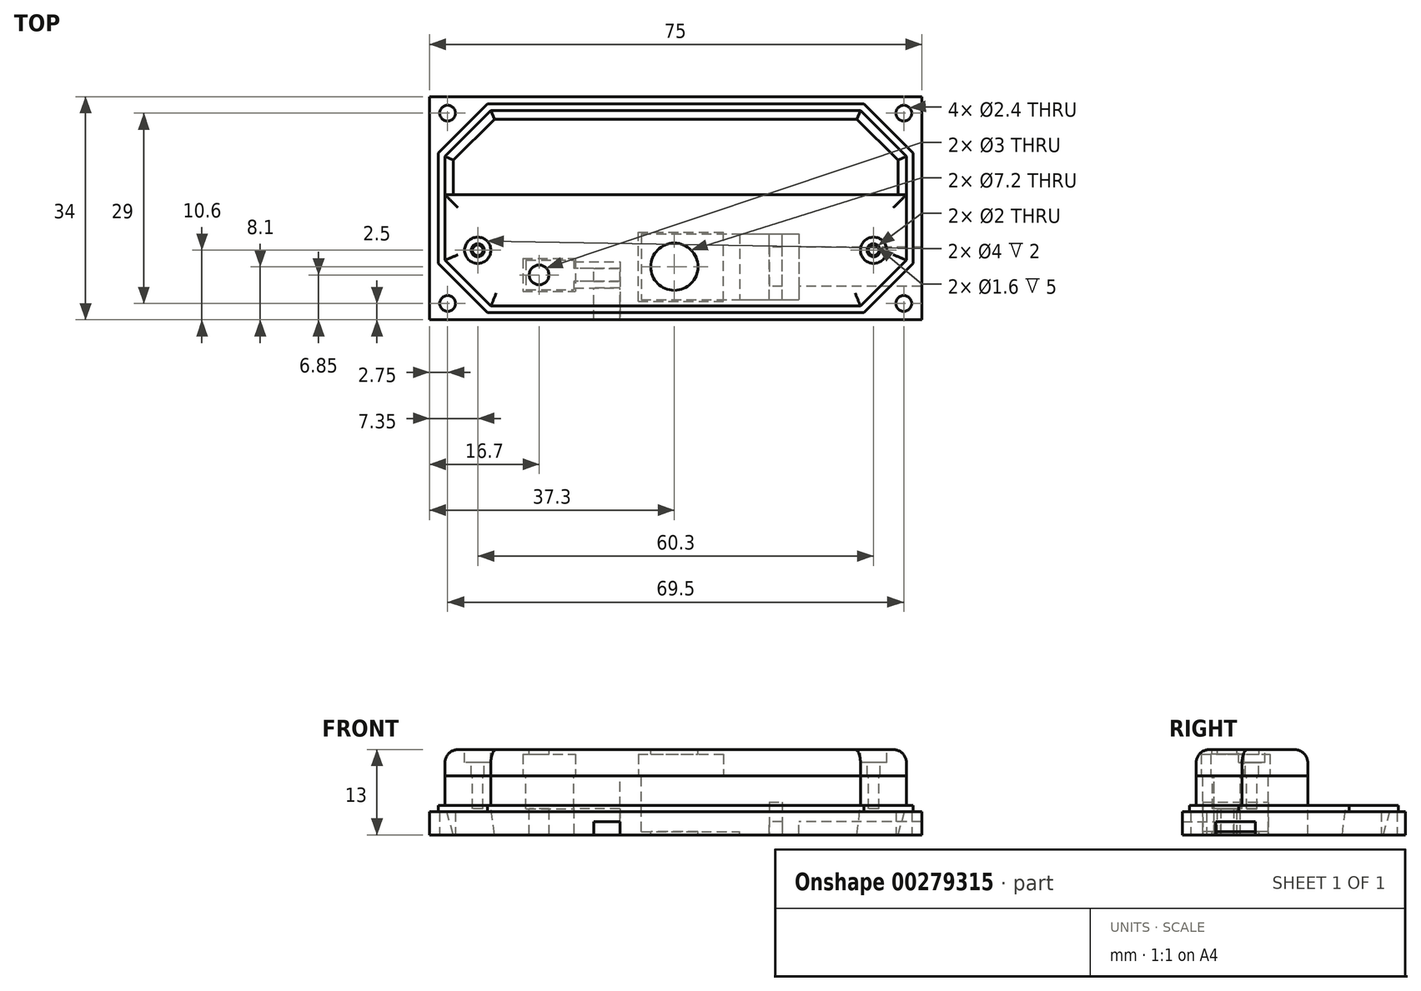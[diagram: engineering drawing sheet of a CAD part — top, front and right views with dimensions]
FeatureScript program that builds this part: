
annotation { "Feature Type Name" : "Feature", "Feature Type Description" : "" }
export const myFeature = defineFeature(function(context is Context, id is Id, definition is map)
    precondition{}
    {
        {
            var Q0;
            Q0=qCreatedBy(makeId("Top.planeOp"),FACE);
            var sketch = newSketch(context, id + "F0", { "sketchPlane" : qUnion([Q0])});
            skLineSegment(sketch, "E0.bottom", {"start": v(37.5, -17) * mm, "end": v(-37.5, -17) * mm});
            skLineSegment(sketch, "E0.top", {"start": v(37.5, 17) * mm, "end": v(-37.5, 17) * mm});
            skLineSegment(sketch, "E0.left", {"start": v(37.5, -17) * mm, "end": v(37.5, 17) * mm});
            skLineSegment(sketch, "E0.right", {"start": v(-37.5, -17) * mm, "end": v(-37.5, 17) * mm});
            skPoint(sketch, "E0.middle", {"position": v(0, 0) * mm});
            skLineSegment(sketch, "E1.bottom", {"start": v(-28.65, 15.9) * mm, "end": v(28.65, 15.9) * mm, "construction": true});
            skLineSegment(sketch, "E1.top", {"start": v(-28.65, -15.9) * mm, "end": v(28.65, -15.9) * mm, "construction": true});
            skLineSegment(sketch, "E1.left", {"start": v(-36.15, 8.4) * mm, "end": v(-36.15, -8.4) * mm, "construction": true});
            skLineSegment(sketch, "E1.right", {"start": v(36.15, 8.4) * mm, "end": v(36.15, -8.4) * mm, "construction": true});
            skLineSegment(sketch, "E2", {"start": v(-36.15, 8.4) * mm, "end": v(-28.65, 15.9) * mm, "construction": true});
            skLineSegment(sketch, "E3", {"start": v(28.65, 15.9) * mm, "end": v(36.15, 8.4) * mm, "construction": true});
            skLineSegment(sketch, "E4", {"start": v(36.15, -8.4) * mm, "end": v(28.65, -15.9) * mm, "construction": true});
            skLineSegment(sketch, "E5", {"start": v(-36.15, -8.4) * mm, "end": v(-28.65, -15.9) * mm, "construction": true});
            skCircle(sketch, "E6", {"center": v(-34.75, 14.5) * mm, "radius": 1.2 * mm});
            skCircle(sketch, "E7", {"center": v(34.75, 14.5) * mm, "radius": 1.2 * mm});
            skCircle(sketch, "E8", {"center": v(-34.75, -14.5) * mm, "radius": 1.2 * mm});
            skCircle(sketch, "E9", {"center": v(34.75, -14.5) * mm, "radius": 1.2 * mm});
            skLineSegment(sketch, "E10", {"start": v(0, -47.1) * mm, "end": v(0, -78.86) * mm, "construction": true});
            skSolve(sketch);
        }
        {
            var Q0;
            Q0 = qSketchRegion(id + "F0", true);
            extrude(context, id + "F1", {"entities" : qUnion([Q0]), "depth" : 3.5 * mm});
        }
        {
            var Q0;
            Q0=makeQuery(id+"F1.opExtrude","CAP_FACE",FACE,{"disambiguationData":[OSD([sQuery(id+"F0.wireOp",EDGE,"E0.bottom"),sQuery(id+"F0.wireOp",EDGE,"E0.top"),sQuery(id+"F0.wireOp",EDGE,"E0.left"),sQuery(id+"F0.wireOp",EDGE,"E0.right"),sQuery(id+"F0.wireOp",EDGE,"E6"),sQuery(id+"F0.wireOp",EDGE,"E7"),sQuery(id+"F0.wireOp",EDGE,"E8"),sQuery(id+"F0.wireOp",EDGE,"E9")])],"isStart":false});
            var sketch = newSketch(context, id + "F2", { "sketchPlane" : qUnion([Q0])});
            skLineSegment(sketch, "E11.bottom", {"start": v(-28.65, 15.9) * mm, "end": v(28.65, 15.9) * mm});
            skLineSegment(sketch, "E11.top", {"start": v(-28.65, -15.9) * mm, "end": v(28.65, -15.9) * mm});
            skLineSegment(sketch, "E11.left", {"start": v(-36.15, 8.4) * mm, "end": v(-36.15, -8.4) * mm});
            skLineSegment(sketch, "E11.right", {"start": v(36.15, 8.4) * mm, "end": v(36.15, -8.4) * mm});
            skLineSegment(sketch, "E12", {"start": v(-36.15, 8.4) * mm, "end": v(-28.65, 15.9) * mm});
            skLineSegment(sketch, "E13", {"start": v(28.65, 15.9) * mm, "end": v(36.15, 8.4) * mm});
            skLineSegment(sketch, "E14", {"start": v(36.15, -8.4) * mm, "end": v(28.65, -15.9) * mm});
            skLineSegment(sketch, "E15", {"start": v(-36.15, -8.4) * mm, "end": v(-28.65, -15.9) * mm});
            skSolve(sketch);
        }
        {
            var Q0;
            Q0 = qSketchRegion(id + "F2", true);
            extrude(context, id + "F3", {"entities" : qUnion([Q0]), "operationType" : NewBodyOperationType.ADD, "depth" : 1 * mm});
        }
        {
            var Q0;
            Q0=makeQuery(id+"F3.opExtrude","CAP_FACE",FACE,{"disambiguationData":[OSD([sQuery(id+"F2.wireOp",EDGE,"E11.bottom"),sQuery(id+"F2.wireOp",EDGE,"E11.top"),sQuery(id+"F2.wireOp",EDGE,"E11.left"),sQuery(id+"F2.wireOp",EDGE,"E11.right"),sQuery(id+"F2.wireOp",EDGE,"E12"),sQuery(id+"F2.wireOp",EDGE,"E13"),sQuery(id+"F2.wireOp",EDGE,"E14"),sQuery(id+"F2.wireOp",EDGE,"E15")])],"isStart":false});
            var sketch = newSketch(context, id + "F4", { "sketchPlane" : qUnion([Q0])});
            skLineSegment(sketch, "E16.bottom", {"start": v(-28.15, 14.9) * mm, "end": v(28.15, 14.9) * mm});
            skLineSegment(sketch, "E16.top", {"start": v(-28.15, -14.9) * mm, "end": v(28.15, -14.9) * mm});
            skLineSegment(sketch, "E16.left", {"start": v(-35.15, 7.9) * mm, "end": v(-35.15, -7.9) * mm});
            skLineSegment(sketch, "E16.right", {"start": v(35.15, 7.9) * mm, "end": v(35.15, -7.9) * mm});
            skLineSegment(sketch, "E17", {"start": v(-35.15, 7.9) * mm, "end": v(-28.15, 14.9) * mm});
            skLineSegment(sketch, "E18", {"start": v(28.15, 14.9) * mm, "end": v(35.15, 7.9) * mm});
            skLineSegment(sketch, "E19", {"start": v(35.15, -7.9) * mm, "end": v(28.15, -14.9) * mm});
            skLineSegment(sketch, "E20", {"start": v(-35.15, -7.9) * mm, "end": v(-28.15, -14.9) * mm});
            skSolve(sketch);
        }
        {
            var Q0;
            Q0 = qSketchRegion(id + "F4", true);
            extrude(context, id + "F5", {"entities" : qUnion([Q0]), "operationType" : NewBodyOperationType.REMOVE, "oppositeDirection" : true, "depth" : 5 * mm});
        }
        {
            var Q0;
            Q0=qCreatedBy(makeId("Front.planeOp"),FACE);
            cPlane(context, id + "F6", {"entities" : qUnion([Q0]), "cplaneType" : CPlaneType.OFFSET, "offset" : 2.1 * mm, "oppositeDirection" : true, "width" : 150 * mm, "height" : 150 * mm});
        }
        {
            var Q0;
            Q0=qCreatedBy(id+"F6.planeOp",FACE);
            var sketch = newSketch(context, id + "F7", { "sketchPlane" : qUnion([Q0])});
            skLineSegment(sketch, "E21", {"start": v(-35.15, 4.5) * mm, "end": v(-35.15, 0) * mm});
            skLineSegment(sketch, "E22", {"start": v(-33.85, 0) * mm, "end": v(-35.15, 0) * mm});
            skLineSegment(sketch, "E23", {"start": v(-33.85, 0) * mm, "end": v(-35.15, 4.5) * mm});
            skSolve(sketch);
        }
        {
            var Q0;
            Q0=makeQuery(id+"F3.opExtrude","CAP_FACE",FACE,{"disambiguationData":[OSD([sQuery(id+"F2.wireOp",EDGE,"E11.bottom"),sQuery(id+"F2.wireOp",EDGE,"E11.top"),sQuery(id+"F2.wireOp",EDGE,"E11.left"),sQuery(id+"F2.wireOp",EDGE,"E11.right"),sQuery(id+"F2.wireOp",EDGE,"E12"),sQuery(id+"F2.wireOp",EDGE,"E13"),sQuery(id+"F2.wireOp",EDGE,"E14"),sQuery(id+"F2.wireOp",EDGE,"E15")])],"isStart":false});
            var sketch = newSketch(context, id + "F8", { "sketchPlane" : qUnion([Q0])});
            skLineSegment(sketch, "E24.bottom", {"start": v(-28.15, 14.9) * mm, "end": v(28.15, 14.9) * mm});
            skLineSegment(sketch, "E24.left", {"start": v(-35.15, 7.9) * mm, "end": v(-35.15, 2.1) * mm});
            skLineSegment(sketch, "E24.right", {"start": v(35.15, 7.9) * mm, "end": v(35.15, 2.1) * mm});
            skLineSegment(sketch, "E25", {"start": v(-35.15, 7.9) * mm, "end": v(-28.15, 14.9) * mm});
            skLineSegment(sketch, "E26", {"start": v(28.15, 14.9) * mm, "end": v(35.15, 7.9) * mm});
            skSolve(sketch);
        }
        {
            var Q0;
            Q0 = qSketchRegion(id + "F7", true);
            var Q1;
            Q1 = qConstructionFilter(qBodyType(qCreatedBy(id + "F8" ,EDGE), BodyType.WIRE), ConstructionObject.NO);
            sweep(context, id + "F9", {"operationType" : NewBodyOperationType.ADD, "profiles" : qUnion([Q0]), "path" : qUnion([Q1])});
        }
        {
            var Q0;
            Q0=qCreatedBy(makeId("Top.planeOp"),FACE);
            var sketch = newSketch(context, id + "F10", { "sketchPlane" : qUnion([Q0])});
            skLineSegment(sketch, "E27.top", {"start": v(-28.15, -14.9) * mm, "end": v(28.15, -14.9) * mm});
            skLineSegment(sketch, "E27.left", {"start": v(-35.15, 2.1) * mm, "end": v(-35.15, -7.9) * mm});
            skLineSegment(sketch, "E27.right", {"start": v(35.15, 2.1) * mm, "end": v(35.15, -7.9) * mm});
            skLineSegment(sketch, "E28", {"start": v(35.15, -7.9) * mm, "end": v(28.15, -14.9) * mm});
            skLineSegment(sketch, "E29", {"start": v(-35.15, -7.9) * mm, "end": v(-28.15, -14.9) * mm});
            skLineSegment(sketch, "E30", {"start": v(-35.15, 2.1) * mm, "end": v(35.15, 2.1) * mm});
            skSolve(sketch);
        }
        {
            var Q0;
            Q0 = qSketchRegion(id + "F10", true);
            extrude(context, id + "F11", {"entities" : qUnion([Q0]), "operationType" : NewBodyOperationType.ADD, "depth" : 9 * mm});
        }
        {
            var Q0;
            Q0=makeQuery(id+"F11.opExtrude","CAP_FACE",FACE,{"disambiguationData":[OSD([sQuery(id+"F10.wireOp",EDGE,"E27.top"),sQuery(id+"F10.wireOp",EDGE,"E27.left"),sQuery(id+"F10.wireOp",EDGE,"E27.right"),sQuery(id+"F10.wireOp",EDGE,"E28"),sQuery(id+"F10.wireOp",EDGE,"E29"),sQuery(id+"F10.wireOp",EDGE,"E30")])],"isStart":false});
            var sketch = newSketch(context, id + "F12", { "sketchPlane" : qUnion([Q0])});
            skLineSegment(sketch, "E31.bottom", {"start": v(-5.25, -3.9) * mm, "end": v(9.75, -3.9) * mm});
            skLineSegment(sketch, "E31.top", {"start": v(-5.25, -13.9) * mm, "end": v(9.75, -13.9) * mm});
            skLineSegment(sketch, "E31.left", {"start": v(-5.25, -3.9) * mm, "end": v(-5.25, -13.9) * mm});
            skLineSegment(sketch, "E31.right", {"start": v(9.75, -3.9) * mm, "end": v(9.75, -13.9) * mm});
            skSolve(sketch);
        }
        {
            var Q0;
            Q0 = qSketchRegion(id + "F12", true);
            extrude(context, id + "F13", {"entities" : qUnion([Q0]), "operationType" : NewBodyOperationType.REMOVE, "oppositeDirection" : true, "depth" : 8.5 * mm});
        }
        {
            var Q0;
            Q0=makeQuery(id+"F11.opExtrude","CAP_FACE",FACE,{"disambiguationData":[OSD([sQuery(id+"F10.wireOp",EDGE,"E27.top"),sQuery(id+"F10.wireOp",EDGE,"E27.left"),sQuery(id+"F10.wireOp",EDGE,"E27.right"),sQuery(id+"F10.wireOp",EDGE,"E28"),sQuery(id+"F10.wireOp",EDGE,"E29"),sQuery(id+"F10.wireOp",EDGE,"E30")])],"isStart":false});
            var sketch = newSketch(context, id + "F14", { "sketchPlane" : qUnion([Q0])});
            skLineSegment(sketch, "E32.bottom", {"start": v(-22.8, -7.9) * mm, "end": v(-15.5, -7.9) * mm});
            skLineSegment(sketch, "E32.top", {"start": v(-22.8, -12.4) * mm, "end": v(-15.5, -12.4) * mm});
            skLineSegment(sketch, "E32.left", {"start": v(-22.8, -7.9) * mm, "end": v(-22.8, -12.4) * mm});
            skLineSegment(sketch, "E32.right", {"start": v(-15.5, -7.9) * mm, "end": v(-15.5, -12.4) * mm});
            skSolve(sketch);
        }
        {
            var Q0;
            Q0 = qSketchRegion(id + "F14", true);
            extrude(context, id + "F15", {"entities" : qUnion([Q0]), "operationType" : NewBodyOperationType.REMOVE, "oppositeDirection" : true, "depth" : 5 * mm});
        }
        {
            var Q0;
            Q0=makeQuery(id+"F11.opExtrude","CAP_FACE",FACE,{"disambiguationData":[OSD([sQuery(id+"F10.wireOp",EDGE,"E27.top"),sQuery(id+"F10.wireOp",EDGE,"E27.left"),sQuery(id+"F10.wireOp",EDGE,"E27.right"),sQuery(id+"F10.wireOp",EDGE,"E28"),sQuery(id+"F10.wireOp",EDGE,"E29"),sQuery(id+"F10.wireOp",EDGE,"E30")])],"isStart":false});
            var sketch = newSketch(context, id + "F16", { "sketchPlane" : qUnion([Q0])});
            skLineSegment(sketch, "E33.bottom", {"start": v(9.75, -3.9) * mm, "end": v(18.75, -3.9) * mm});
            skLineSegment(sketch, "E33.top", {"start": v(9.75, -13.9) * mm, "end": v(18.75, -13.9) * mm});
            skLineSegment(sketch, "E33.left", {"start": v(9.75, -3.9) * mm, "end": v(9.75, -13.9) * mm});
            skLineSegment(sketch, "E33.right", {"start": v(18.75, -3.9) * mm, "end": v(18.75, -13.9) * mm});
            skLineSegment(sketch, "E34.bottom", {"start": v(-15.5, -8.15) * mm, "end": v(-8.5, -8.15) * mm});
            skLineSegment(sketch, "E34.top", {"start": v(-15.5, -12.15) * mm, "end": v(-8.5, -12.15) * mm});
            skLineSegment(sketch, "E34.left", {"start": v(-15.5, -8.15) * mm, "end": v(-15.5, -12.15) * mm});
            skLineSegment(sketch, "E34.right", {"start": v(-8.5, -8.15) * mm, "end": v(-8.5, -12.15) * mm});
            skSolve(sketch);
        }
        {
            var Q0;
            Q0 = qSketchRegion(id + "F16", true);
            extrude(context, id + "F17", {"entities" : qUnion([Q0]), "operationType" : NewBodyOperationType.REMOVE, "oppositeDirection" : true, "depth" : 25 * mm});
        }
        {
            var Q0;
            Q0=makeQuery(id+"F17.boolean.opBoolean","MERGE",FACE,{"derivedFrom":[makeQuery(id+"F13.boolean.opBoolean","COPY",FACE,{"derivedFrom":makeQuery(id+"F13.opExtrude","SWEPT_FACE",FACE,{"disambiguationData":[OSD([sQuery(id+"F12.wireOp",EDGE,"E31.bottom")])]})}),makeQuery(id+"F17.opExtrude","SWEPT_FACE",FACE,{"disambiguationData":[OSD([sQuery(id+"F16.wireOp",EDGE,"E33.bottom")])]})]});
            var sketch = newSketch(context, id + "F18", { "sketchPlane" : qUnion([Q0])});
            skLineSegment(sketch, "E35.bottom", {"start": v(14.25, 5) * mm, "end": v(16.25, 5) * mm});
            skLineSegment(sketch, "E35.top", {"start": v(14.25, 0) * mm, "end": v(16.25, 0) * mm});
            skLineSegment(sketch, "E35.left", {"start": v(14.25, 5) * mm, "end": v(14.25, 0) * mm});
            skLineSegment(sketch, "E35.right", {"start": v(16.25, 5) * mm, "end": v(16.25, 0) * mm});
            skSolve(sketch);
        }
        {
            var Q0;
            Q0 = qSketchRegion(id + "F18", true);
            extrude(context, id + "F19", {"entities" : qUnion([Q0]), "operationType" : NewBodyOperationType.ADD, "depth" : 10 * mm});
        }
        {
            var Q0;
            Q0=makeQuery(id+"F19.opExtrude","SWEPT_FACE",FACE,{"disambiguationData":[OSD([sQuery(id+"F18.wireOp",EDGE,"E35.left")])]});
            var sketch = newSketch(context, id + "F20", { "sketchPlane" : qUnion([Q0])});
            skLineSegment(sketch, "E36.bottom", {"start": v(5.9, 0) * mm, "end": v(11.9, 0) * mm});
            skLineSegment(sketch, "E36.top", {"start": v(5.9, 2) * mm, "end": v(11.9, 2) * mm});
            skLineSegment(sketch, "E36.left", {"start": v(5.9, 0) * mm, "end": v(5.9, 2) * mm});
            skLineSegment(sketch, "E36.right", {"start": v(11.9, 0) * mm, "end": v(11.9, 2) * mm});
            skSolve(sketch);
        }
        {
            var Q0;
            Q0 = qSketchRegion(id + "F20", true);
            extrude(context, id + "F21", {"entities" : qUnion([Q0]), "operationType" : NewBodyOperationType.REMOVE, "oppositeDirection" : true, "depth" : 25 * mm});
        }
        {
            var Q0;
            Q0=makeQuery(id+"F11.opExtrude","CAP_FACE",FACE,{"disambiguationData":[OSD([sQuery(id+"F10.wireOp",EDGE,"E27.top"),sQuery(id+"F10.wireOp",EDGE,"E27.left"),sQuery(id+"F10.wireOp",EDGE,"E27.right"),sQuery(id+"F10.wireOp",EDGE,"E28"),sQuery(id+"F10.wireOp",EDGE,"E29"),sQuery(id+"F10.wireOp",EDGE,"E30")])],"isStart":false});
            var sketch = newSketch(context, id + "F22", { "sketchPlane" : qUnion([Q0])});
            skCircle(sketch, "E37", {"center": v(-30.15, -6.4) * mm, "radius": 0.8 * mm});
            skCircle(sketch, "E38", {"center": v(30.15, -6.4) * mm, "radius": 0.8 * mm});
            skSolve(sketch);
        }
        {
            var Q0;
            Q0 = qSketchRegion(id + "F22", true);
            extrude(context, id + "F23", {"entities" : qUnion([Q0]), "operationType" : NewBodyOperationType.REMOVE, "oppositeDirection" : true, "depth" : 5 * mm});
        }
        {
            var Q0;
            Q0=qCreatedBy(makeId("Top.planeOp"),FACE);
            cPlane(context, id + "F24", {"entities" : qUnion([Q0]), "cplaneType" : CPlaneType.OFFSET, "offset" : 9 * mm, "width" : 150 * mm, "height" : 150 * mm});
        }
        {
            var Q0;
            Q0=qCreatedBy(id+"F24.planeOp",FACE);
            var sketch = newSketch(context, id + "F25", { "sketchPlane" : qUnion([Q0])});
            skLineSegment(sketch, "E39.top", {"start": v(-28.15, -14.9) * mm, "end": v(28.15, -14.9) * mm});
            skLineSegment(sketch, "E39.left", {"start": v(-35.15, 2.1) * mm, "end": v(-35.15, -7.9) * mm});
            skLineSegment(sketch, "E39.right", {"start": v(35.15, 2.1) * mm, "end": v(35.15, -7.9) * mm});
            skLineSegment(sketch, "E40", {"start": v(35.15, -7.9) * mm, "end": v(28.15, -14.9) * mm});
            skLineSegment(sketch, "E41", {"start": v(-35.15, -7.9) * mm, "end": v(-28.15, -14.9) * mm});
            skLineSegment(sketch, "E42", {"start": v(-35.15, 2.1) * mm, "end": v(35.15, 2.1) * mm});
            skSolve(sketch);
        }
        {
            var Q0;
            Q0 = qSketchRegion(id + "F25", true);
            extrude(context, id + "F26", {"entities" : qUnion([Q0]), "depth" : 4 * mm});
        }
        {
            var Q0;
            Q0=makeQuery(id+"F26.opExtrude","CAP_FACE",FACE,{"disambiguationData":[OSD([sQuery(id+"F25.wireOp",EDGE,"E39.top"),sQuery(id+"F25.wireOp",EDGE,"E39.left"),sQuery(id+"F25.wireOp",EDGE,"E39.right"),sQuery(id+"F25.wireOp",EDGE,"E40"),sQuery(id+"F25.wireOp",EDGE,"E41"),sQuery(id+"F25.wireOp",EDGE,"E42")])],"isStart":false});
            var sketch = newSketch(context, id + "F27", { "sketchPlane" : qUnion([Q0])});
            skCircle(sketch, "E43", {"center": v(-0.2, -8.9) * mm, "radius": 3.6 * mm});
            skCircle(sketch, "E44", {"center": v(-20.8, -10.15) * mm, "radius": 1.5 * mm});
            skSolve(sketch);
        }
        {
            var Q0;
            Q0 = qSketchRegion(id + "F27", true);
            extrude(context, id + "F28", {"entities" : qUnion([Q0]), "operationType" : NewBodyOperationType.REMOVE, "oppositeDirection" : true, "depth" : 25 * mm});
        }
        {
            var Q0;
            Q0=makeQuery(id+"F26.opExtrude","CAP_FACE",FACE,{"disambiguationData":[OSD([sQuery(id+"F25.wireOp",EDGE,"E39.top"),sQuery(id+"F25.wireOp",EDGE,"E39.left"),sQuery(id+"F25.wireOp",EDGE,"E39.right"),sQuery(id+"F25.wireOp",EDGE,"E40"),sQuery(id+"F25.wireOp",EDGE,"E41"),sQuery(id+"F25.wireOp",EDGE,"E42")])],"isStart":true});
            var sketch = newSketch(context, id + "F29", { "sketchPlane" : qUnion([Q0])});
            skLineSegment(sketch, "E45.bottom", {"start": v(-5.7, 14.15) * mm, "end": v(7.3, 14.15) * mm});
            skLineSegment(sketch, "E45.top", {"start": v(-5.7, 3.65) * mm, "end": v(7.3, 3.65) * mm});
            skLineSegment(sketch, "E45.left", {"start": v(-5.7, 14.15) * mm, "end": v(-5.7, 3.65) * mm});
            skLineSegment(sketch, "E45.right", {"start": v(7.3, 14.15) * mm, "end": v(7.3, 3.65) * mm});
            skPoint(sketch, "E45.middle", {"position": v(0.8, 8.9) * mm});
            skLineSegment(sketch, "E46.bottom", {"start": v(-23.3, 7.65) * mm, "end": v(-15.3, 7.65) * mm});
            skLineSegment(sketch, "E46.top", {"start": v(-23.3, 12.65) * mm, "end": v(-15.3, 12.65) * mm});
            skLineSegment(sketch, "E46.left", {"start": v(-23.3, 7.65) * mm, "end": v(-23.3, 12.65) * mm});
            skLineSegment(sketch, "E46.right", {"start": v(-15.3, 7.65) * mm, "end": v(-15.3, 12.65) * mm});
            skCircle(sketch, "E47", {"center": v(-20.8, 10.15) * mm, "radius": 1.5 * mm, "construction": true});
            skSolve(sketch);
        }
        {
            var Q0;
            Q0 = qSketchRegion(id + "F29", true);
            extrude(context, id + "F30", {"entities" : qUnion([Q0]), "operationType" : NewBodyOperationType.REMOVE, "oppositeDirection" : true, "depth" : 3.3 * mm});
        }
        {
            var Q0;
            Q0=makeQuery(id+"F17.boolean.opBoolean","COPY",FACE,{"derivedFrom":makeQuery(id+"F17.opExtrude","SWEPT_FACE",FACE,{"disambiguationData":[OSD([sQuery(id+"F16.wireOp",EDGE,"E34.left")])]})});
            var sketch = newSketch(context, id + "F31", { "sketchPlane" : qUnion([Q0])});
            skLineSegment(sketch, "E48.bottom", {"start": v(-11.15, 4) * mm, "end": v(-9.15, 4) * mm});
            skLineSegment(sketch, "E48.top", {"start": v(-11.15, 0) * mm, "end": v(-9.15, 0) * mm});
            skLineSegment(sketch, "E48.left", {"start": v(-11.15, 4) * mm, "end": v(-11.15, 0) * mm});
            skLineSegment(sketch, "E48.right", {"start": v(-9.15, 4) * mm, "end": v(-9.15, 0) * mm});
            skSolve(sketch);
        }
        {
            var Q0;
            Q0 = qSketchRegion(id + "F31", true);
            extrude(context, id + "F32", {"entities" : qUnion([Q0]), "operationType" : NewBodyOperationType.ADD, "depth" : 7 * mm});
        }
        {
            var Q0;
            Q0=makeQuery(id+"F32.opExtrude","SWEPT_FACE",FACE,{"disambiguationData":[OSD([sQuery(id+"F31.wireOp",EDGE,"E48.right")])]});
            var sketch = newSketch(context, id + "F33", { "sketchPlane" : qUnion([Q0])});
            skLineSegment(sketch, "E49.bottom", {"start": v(12.5, 0) * mm, "end": v(8.5, 0) * mm});
            skLineSegment(sketch, "E49.top", {"start": v(12.5, 2) * mm, "end": v(8.5, 2) * mm});
            skLineSegment(sketch, "E49.left", {"start": v(12.5, 0) * mm, "end": v(12.5, 2) * mm});
            skLineSegment(sketch, "E49.right", {"start": v(8.5, 0) * mm, "end": v(8.5, 2) * mm});
            skSolve(sketch);
        }
        {
            var Q0;
            Q0 = qSketchRegion(id + "F33", true);
            extrude(context, id + "F34", {"entities" : qUnion([Q0]), "operationType" : NewBodyOperationType.REMOVE, "oppositeDirection" : true, "depth" : 25 * mm});
        }
        {
            var Q0;
            Q0=makeQuery(id+"F26.opExtrude","CAP_FACE",FACE,{"disambiguationData":[OSD([sQuery(id+"F25.wireOp",EDGE,"E39.top"),sQuery(id+"F25.wireOp",EDGE,"E39.left"),sQuery(id+"F25.wireOp",EDGE,"E39.right"),sQuery(id+"F25.wireOp",EDGE,"E40"),sQuery(id+"F25.wireOp",EDGE,"E41"),sQuery(id+"F25.wireOp",EDGE,"E42")])],"isStart":false});
            var sketch = newSketch(context, id + "F35", { "sketchPlane" : qUnion([Q0])});
            skCircle(sketch, "E50", {"center": v(-30.15, -6.4) * mm, "radius": 1 * mm, "construction": true});
            skCircle(sketch, "E51", {"center": v(30.15, -6.4) * mm, "radius": 1 * mm, "construction": true});
            skSolve(sketch);
        }
        {
            var Q0;
            Q0=sQuery(id+"F35.wireOp",VERTEX,"E50.center");
            var Q1;
            Q1=sQuery(id+"F35.wireOp",VERTEX,"E51.center");
            var Q2;
            Q2=makeQuery(id+"F26.opExtrude","SWEPT_BODY",BODY,{"disambiguationData":[OSD([sQuery(id+"F25.wireOp",EDGE,"E39.top"),sQuery(id+"F25.wireOp",EDGE,"E39.left"),sQuery(id+"F25.wireOp",EDGE,"E39.right"),sQuery(id+"F25.wireOp",EDGE,"E40"),sQuery(id+"F25.wireOp",EDGE,"E41"),sQuery(id+"F25.wireOp",EDGE,"E42")])]});
            hole(context, id + "F36", {"style" : HoleStyle.C_BORE, "endStyle" : HoleEndStyle.BLIND, "holeDiameter" : 2 * mm, "cBoreDiameter" : 4 * mm, "cBoreDepth" : 2 * mm, "holeDepth" : 10 * mm, "tappedDepth" : 12 * mm, "tapClearance" : 3, "locations" : qUnion([Q0, Q1]), "scope" : qUnion([Q2])});
        }
        {
            var Q0;
            Q0=makeQuery(id+"F26.opExtrude","CAP_EDGE",EDGE,{"disambiguationData":[OSD([sQuery(id+"F25.wireOp",EDGE,"E39.top")])],"isStart":false});
            var Q1;
            Q1=makeQuery(id+"F26.opExtrude","CAP_EDGE",EDGE,{"disambiguationData":[OSD([sQuery(id+"F25.wireOp",EDGE,"E41")])],"isStart":false});
            var Q2;
            Q2=makeQuery(id+"F26.opExtrude","CAP_EDGE",EDGE,{"disambiguationData":[OSD([sQuery(id+"F25.wireOp",EDGE,"E39.left")])],"isStart":false});
            var Q3;
            Q3=makeQuery(id+"F26.opExtrude","CAP_EDGE",EDGE,{"disambiguationData":[OSD([sQuery(id+"F25.wireOp",EDGE,"E42")])],"isStart":false});
            var Q4;
            Q4=makeQuery(id+"F26.opExtrude","CAP_EDGE",EDGE,{"disambiguationData":[OSD([sQuery(id+"F25.wireOp",EDGE,"E39.right")])],"isStart":false});
            var Q5;
            Q5=makeQuery(id+"F26.opExtrude","CAP_EDGE",EDGE,{"disambiguationData":[OSD([sQuery(id+"F25.wireOp",EDGE,"E40")])],"isStart":false});
            fillet(context, id + "F37", {"entities" : qUnion([Q0, Q1, Q2, Q3, Q4, Q5]), "radius" : 2 * mm, "tangentPropagation" : true, "allowEdgeOverflow" : false});
        }
    });
